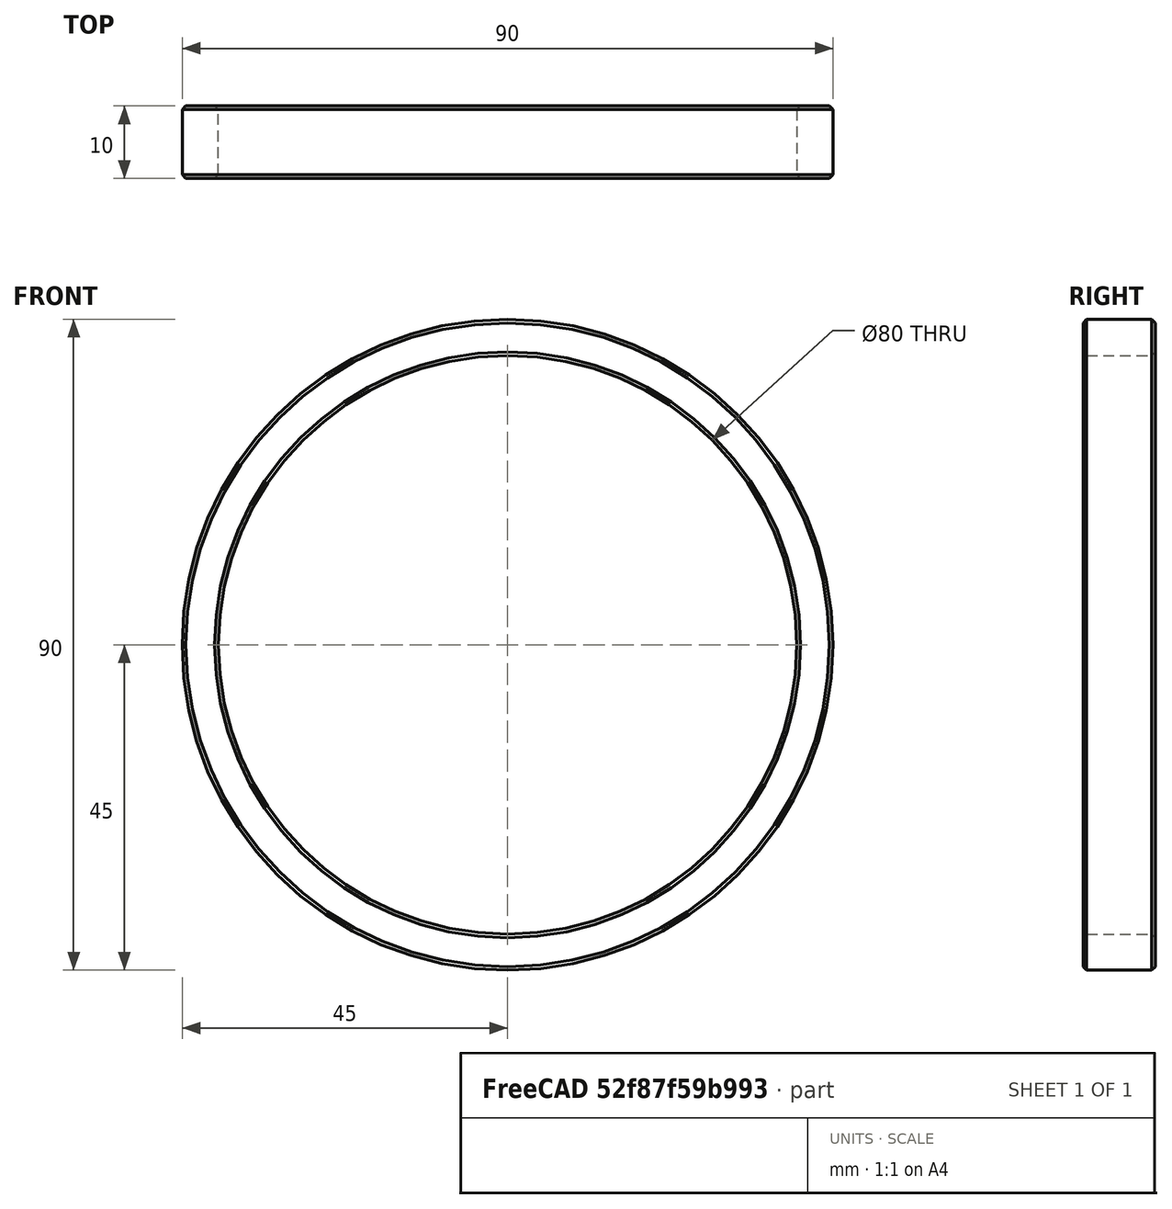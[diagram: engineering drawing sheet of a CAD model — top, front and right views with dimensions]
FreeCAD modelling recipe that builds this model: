
FCSTD DOCUMENT  (FreeCAD 1.0R39109 (Git))
Label: Adjustable_hoop_ring
License: All rights reserved
objects: Sketcher::SketchObject×1, PartDesign::Pad×1, PartDesign::Chamfer×1, PartDesign::Body×1
note: 9 computed .brp shape members not serialized (recipe doc carries the construction recipe); baked Part::Feature solids carry a one-line shape summary decoded from their .brp

FEATURE [Sketcher::SketchObject] Sketch
  ArcFitTolerance = 1e-06
  AttachmentSupport = -> [XZ_Plane]
  FullyConstrained = true
  MakeInternals = false
  MapMode = 5
  Placement = pos=(0,0,0) rot=(1,0,0;1.5708rad)
  sketch-geometry (2):
    g0: Circle CenterX=0 CenterY=0 CenterZ=0 NormalX=0 NormalY=0 NormalZ=1 AngleXU=0 Radius=40
    g1: Circle CenterX=0 CenterY=0 CenterZ=0 NormalX=0 NormalY=0 NormalZ=1 AngleXU=0 Radius=45
  constraints (4):
    c: Diameter(g0) = 80
    c: Coincident(g0,g-1)
    c: Diameter(g1) = 90
    c: Coincident(g1,g0)
FEATURE [PartDesign::Pad] Pad
  Direction = (0,-1,2e-16)
  Length = 10
  Length2 = 10
  Placement = pos=(0,0,0) rot=(1,0,0;1.5708rad)
  Profile = -> Sketch
  ReferenceAxis = -> Sketch [N_Axis]
  Refine = true
  Suppressed = false
  Type = 0
FEATURE [PartDesign::Chamfer] Chamfer
  Angle = 45
  Base = -> Pad [Edge3,Edge6,Edge2,Edge5]
  BaseFeature = -> Pad
  ChamferType = 0
  FlipDirection = false
  Placement = pos=(0,0,0) rot=(1,0,0;1.5708rad)
  Refine = true
  Size = 0.5
  Size2 = 1
  SupportTransform = false
  Suppressed = false
  UseAllEdges = false
FEATURE [PartDesign::Body] Body
  AllowCompound = false
  Group = -> [Sketch,Pad,Chamfer]
  Origin = -> Origin
  Tip = -> Chamfer
